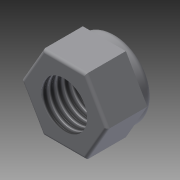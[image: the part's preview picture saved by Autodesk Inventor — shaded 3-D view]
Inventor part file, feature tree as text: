
AUTODESK INVENTOR PART (.ipt)
format: ipt  version: 2014 SP2 (Build 180246200, 246)  size: 142,336 bytes
history: native  units: mm
features: extrude x2, fillet x2, sketch x2, thread x1
ambient origin geometry x8: Origin, YZ Plane, XZ Plane, XY Plane, X Axis, Y Axis, Z Axis, Center Point
bodies: Solid1 (feature_tree)
feature tree (7):
  extrude  "Extrusion1"  Depth=7.0mm
  thread  "Thread1"  [1 undecoded]
  extrude  "Extrusion2"  Depth=2.0mm TaperAngle=0.0deg
  fillet  "Fillet1"  Radius=0.999mm
  fillet  "Fillet2"  Radius=0.5mm
  sketch  "Sketch1"  dims[d0=13.0mm d1=8.0mm d2=7.0mm d3=0.0mm]
  sketch  "Sketch2"  dims[d4=10.0mm d5=0.0mm d6=2.0mm d7=0.0mm d8=0.999mm d9=0.5mm]
note: 1 required parameter value undecoded (feature->parameter linkage not recoverable at this tier; creation-order binding heuristic only, values carry confidence <= 0.55)
